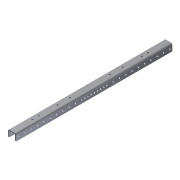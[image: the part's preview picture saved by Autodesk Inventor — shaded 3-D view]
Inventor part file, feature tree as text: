
AUTODESK INVENTOR PART (.ipt)
format: ipt  version: 2011 (Build 150239000, 239)  size: 335,872 bytes
history: native  units: in
note: dims shown in document units (in); Inventor stores cm internally (conversion verified against a paired STEP export)
features: sketch x7, extrude x5, fillet x2, reference x2, pattern_linear x1, plane x1, projected_geometry x1
ambient origin geometry x8: Origin, YZ Plane, XZ Plane, XY Plane, X Axis, Y Axis, Z Axis, Center Point
bodies: Solid1 (feature_tree)
feature tree (19):
  extrude  "Extrusion1"  Depth=1.25in
  fillet  "Fillet1"  Radius=0.125in
  fillet  "Fillet2"  Radius=0.125in
  extrude  "Extrusion2"  TaperAngle=0.0deg  [1 undecoded]
  pattern_linear  "Rectangular Pattern1"  Spacing1=0.5in  [1 undecoded]
  plane  "Work Plane2"
  extrude  "Extrusion5"  Depth=35.0in TaperAngle=0.0deg
  extrude  "Extrusion7"  Depth=13.7795in
  sketch  "Sketch9"  dims[d9=0.125in]
  extrude  "Extrusion8"  Depth=1.0in TaperAngle=0.0deg
  sketch  "Sketch11"  dims[d11=0.5in d12=0.5in d13=35.0in d14=0.0in d15=13.7795in d17=1.0in d37=1.0in d38=0.0in d43=0.25in d44=3.25in d45=1.0in d46=3.0in d47=2.0in d48=3.25in d49=1.0in d50=3.0in d51=2.0in d52=1.0in d53=0.0in d54=24.875in d55=0.25in d56=0.25in d57=1.0in d58=2.0in d59=1.5in d60=0.0in d61=1.9626in d62=2.5in]
  sketch  "Sketch1"  dims[d0=1.0in d1=1.25in d2=0.125in d3=0.125in]
  sketch  "Sketch2"  dims[d4=1.125in d5=0.0in]
  sketch  "Sketch6"  dims[d6=35.0in d7=0.0in]
  sketch  "Sketch8"  dims[d8=0.25in]
  projected_geometry  "Projected Loop1"
  sketch  "Sketch10"  dims[d10=0.25in]
  reference  "Reference1"
  reference  "Reference2"
note: 2 required parameter values undecoded (feature->parameter linkage not recoverable at this tier; creation-order binding heuristic only, values carry confidence <= 0.55)
